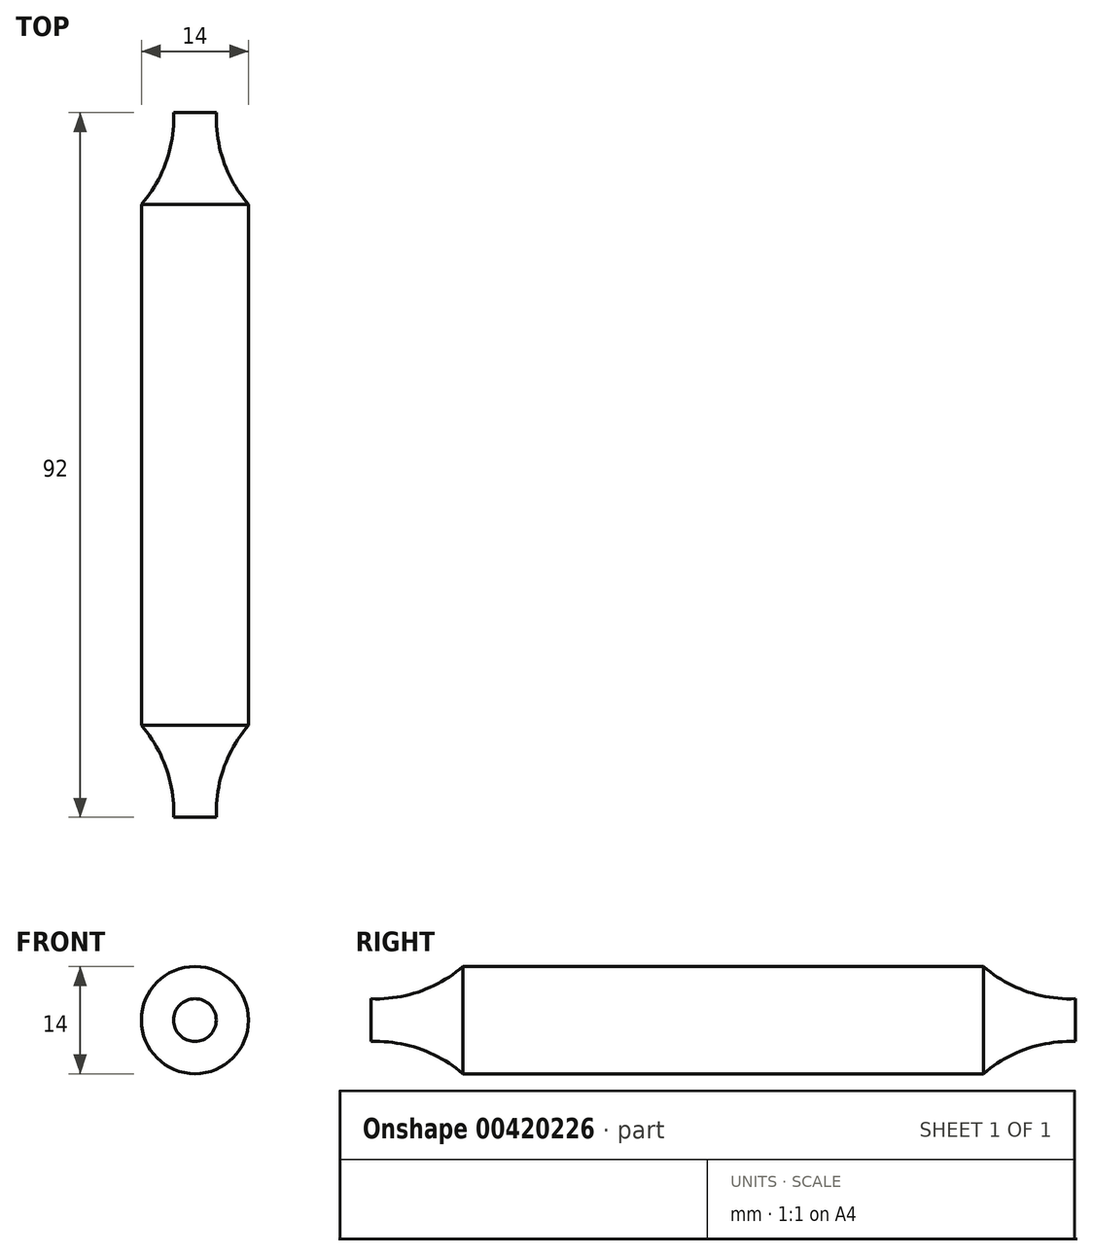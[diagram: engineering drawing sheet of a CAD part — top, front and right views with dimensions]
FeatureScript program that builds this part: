
annotation { "Feature Type Name" : "Feature", "Feature Type Description" : "" }
export const myFeature = defineFeature(function(context is Context, id is Id, definition is map)
    precondition{}
    {
        {
            var Q0;
            Q0=qCreatedBy(makeId("Top.planeOp"),FACE);
            var sketch = newSketch(context, id + "F0", { "sketchPlane" : qUnion([Q0])});
            skLineSegment(sketch, "E0", {"start": v(0, 0) * mm, "end": v(0, -34) * mm});
            skLineSegment(sketch, "E1", {"start": v(7, 12) * mm, "end": v(7, -34) * mm});
            skLineSegment(sketch, "E2", {"start": v(7, 12) * mm, "end": v(4.2, 12) * mm});
            skArc(sketch, "E3", {"start": v(0, 0) * mm, "mid": v(3.24, 5.6) * mm, "end": v(4.2, 12) * mm});
            skLineSegment(sketch, "E4", {"start": v(0, -34) * mm, "end": v(7, -34) * mm});
            skPoint(sketch, "E5.orphan", {"position": v(0, -68) * mm});
            skLineSegment(sketch, "E6.MirrorCS", {"start": v(0, -68) * mm, "end": v(0, -34) * mm});
            skArc(sketch, "E7.MirrorCS", {"start": v(0, -68) * mm, "mid": v(3.24, -73.6) * mm, "end": v(4.2, -80) * mm});
            skLineSegment(sketch, "E8.MirrorCS", {"start": v(7, -80) * mm, "end": v(4.2, -80) * mm});
            skLineSegment(sketch, "E9.MirrorCS", {"start": v(7, -80) * mm, "end": v(7, -34) * mm});
            skSolve(sketch);
        }
        {
            var Q0;
            Q0=makeQuery(id+"F0.imprint","IMPRINT",FACE,{"disambiguationData":[TD([[makeQuery(id+"F0.imprint","IMPRINT",EDGE,{"derivedFrom":sQuery(id+"F0.wireOp",EDGE,"E0")}),1.0]])]});
            var Q1;
            Q1=makeQuery(id+"F0.imprint","IMPRINT",FACE,{"disambiguationData":[TD([[makeQuery(id+"F0.imprint","IMPRINT",EDGE,{"derivedFrom":sQuery(id+"F0.wireOp",EDGE,"E4")}),-1.0]])]});
            var Q2;
            Q2=sQuery(id+"F0.wireOp",EDGE,"E1");
            revolve(context, id + "F1", {"entities" : qUnion([Q0, Q1]), "axis" : qUnion([Q2]), "revolveType" : RevolveType.FULL});
        }
    });
